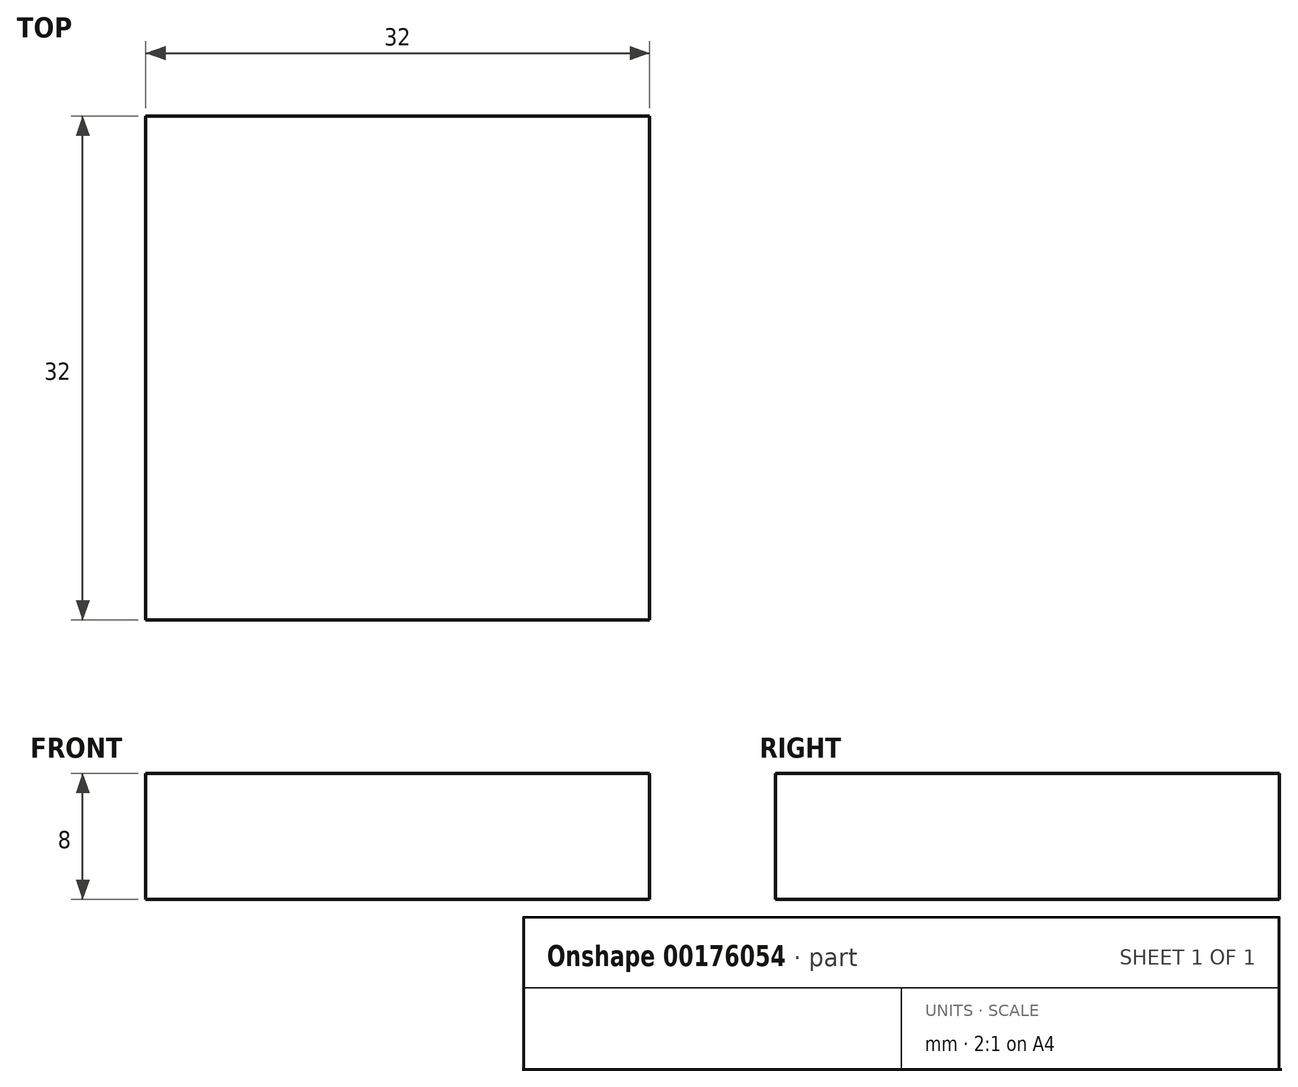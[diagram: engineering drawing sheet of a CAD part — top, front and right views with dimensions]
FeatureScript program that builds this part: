
annotation { "Feature Type Name" : "Feature", "Feature Type Description" : "" }
export const myFeature = defineFeature(function(context is Context, id is Id, definition is map)
    precondition{}
    {
        {
            var Q0;
            Q0=qCreatedBy(makeId("Top.planeOp"),FACE);
            var sketch = newSketch(context, id + "F0", { "sketchPlane" : qUnion([Q0])});
            skLineSegment(sketch, "E0.bottom", {"start": v(16, -16) * mm, "end": v(-16, -16) * mm});
            skLineSegment(sketch, "E0.top", {"start": v(16, 16) * mm, "end": v(-16, 16) * mm});
            skLineSegment(sketch, "E0.left", {"start": v(16, -16) * mm, "end": v(16, 16) * mm});
            skLineSegment(sketch, "E0.right", {"start": v(-16, -16) * mm, "end": v(-16, 16) * mm});
            skPoint(sketch, "E0.middle", {"position": v(0, 0) * mm});
            skSolve(sketch);
        }
        {
            var Q0;
            Q0 = qSketchRegion(id + "F0", true);
            extrude(context, id + "F1", {"entities" : qUnion([Q0]), "depth" : 8 * mm});
        }
    });
